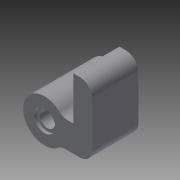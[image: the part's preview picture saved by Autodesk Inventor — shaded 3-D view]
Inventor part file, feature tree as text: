
AUTODESK INVENTOR PART (.ipt)
format: ipt  version: 2015 (Build 190159000, 159)  size: 138,240 bytes
history: native  units: in
note: dims shown in document units (in); Inventor stores cm internally (conversion verified against a paired STEP export)
features: extrude x4, sketch x4, mirror x2, fillet x1, reference x1
ambient origin geometry x8: Origin, YZ Plane, XZ Plane, XY Plane, X Axis, Y Axis, Z Axis, Center Point
bodies: Solid1 (feature_tree)
feature tree (12):
  extrude  "Extrusion1"  Depth=0.9375in TaperAngle=0.0deg
  extrude  "Extrusion2"  Depth=0.4882in TaperAngle=0.0deg
  mirror  "Mirror1"
  extrude  "Extrusion3"  Depth=0.0591in TaperAngle=0.0deg
  extrude  "Extrusion4"  [1 undecoded]
  fillet  "Fillet1"  [1 undecoded]
  mirror  "Mirror2"
  sketch  "Sketch1"  dims[d0=0.375in d1=0.0in d2=0.9375in d3=0.0in]
  reference  "Reference1"
  sketch  "Sketch2"  dims[d4=0.3125in d5=0.4882in d6=0.0in]
  sketch  "Sketch3"  dims[d7=0.4331in d8=0.0591in d9=0.0in]
  sketch  "Sketch4"  dims[d10=0.25in]
note: 2 required parameter values undecoded (feature->parameter linkage not recoverable at this tier; creation-order binding heuristic only, values carry confidence <= 0.55)
